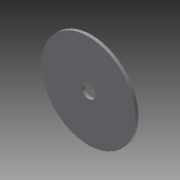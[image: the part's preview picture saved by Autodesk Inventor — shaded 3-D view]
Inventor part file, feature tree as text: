
AUTODESK INVENTOR PART (.ipt)
format: ipt  version: 2014 (Build 180170000, 170)  size: 72,704 bytes
history: native  units: mm
features: extrude x1, sketch x1
ambient origin geometry x8: Origin, YZ Plane, XZ Plane, XY Plane, X Axis, Y Axis, Z Axis, Center Point
bodies: Volumenkörper1 (feature_tree)
feature tree (2):
  extrude  "Extrusion1"  Depth=1.5mm
  sketch  "Skizze1"  dims[d0=47.0mm d1=7.0mm d2=1.5mm d3=0.0mm]
